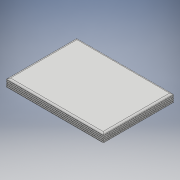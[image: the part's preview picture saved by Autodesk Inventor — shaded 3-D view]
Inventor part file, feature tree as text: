
AUTODESK INVENTOR PART (.ipt)
format: ipt  version: 2018 (Build 220112000, 112)  size: 137,728 bytes
history: native  units: mm
features: extrude x2, sketch x2, fillet x1, pattern_linear x1
ambient origin geometry x8: Origin, YZ Plane, XZ Plane, XY Plane, X Axis, Y Axis, Z Axis, Center Point
bodies: Solid1 (feature_tree)
feature tree (6):
  extrude  "Extrusion1"  Depth=162.0mm
  extrude  "Extrusion2"  Depth=14.1mm
  fillet  "Fillet1"  Radius=160.0mm
  pattern_linear  "Rectangular Pattern1"  Spacing1=3.0mm  [1 undecoded]
  sketch  "Sketch1"  dims[d0=223.0mm d1=162.0mm]
  sketch  "Sketch2"  dims[d2=0.5mm d3=0.0mm d4=220.0mm d5=160.0mm d6=3.0mm d7=0.0mm d8=4.0mm d9=50.0mm d11=14.1mm]
note: 1 required parameter value undecoded (feature->parameter linkage not recoverable at this tier; creation-order binding heuristic only, values carry confidence <= 0.55)
